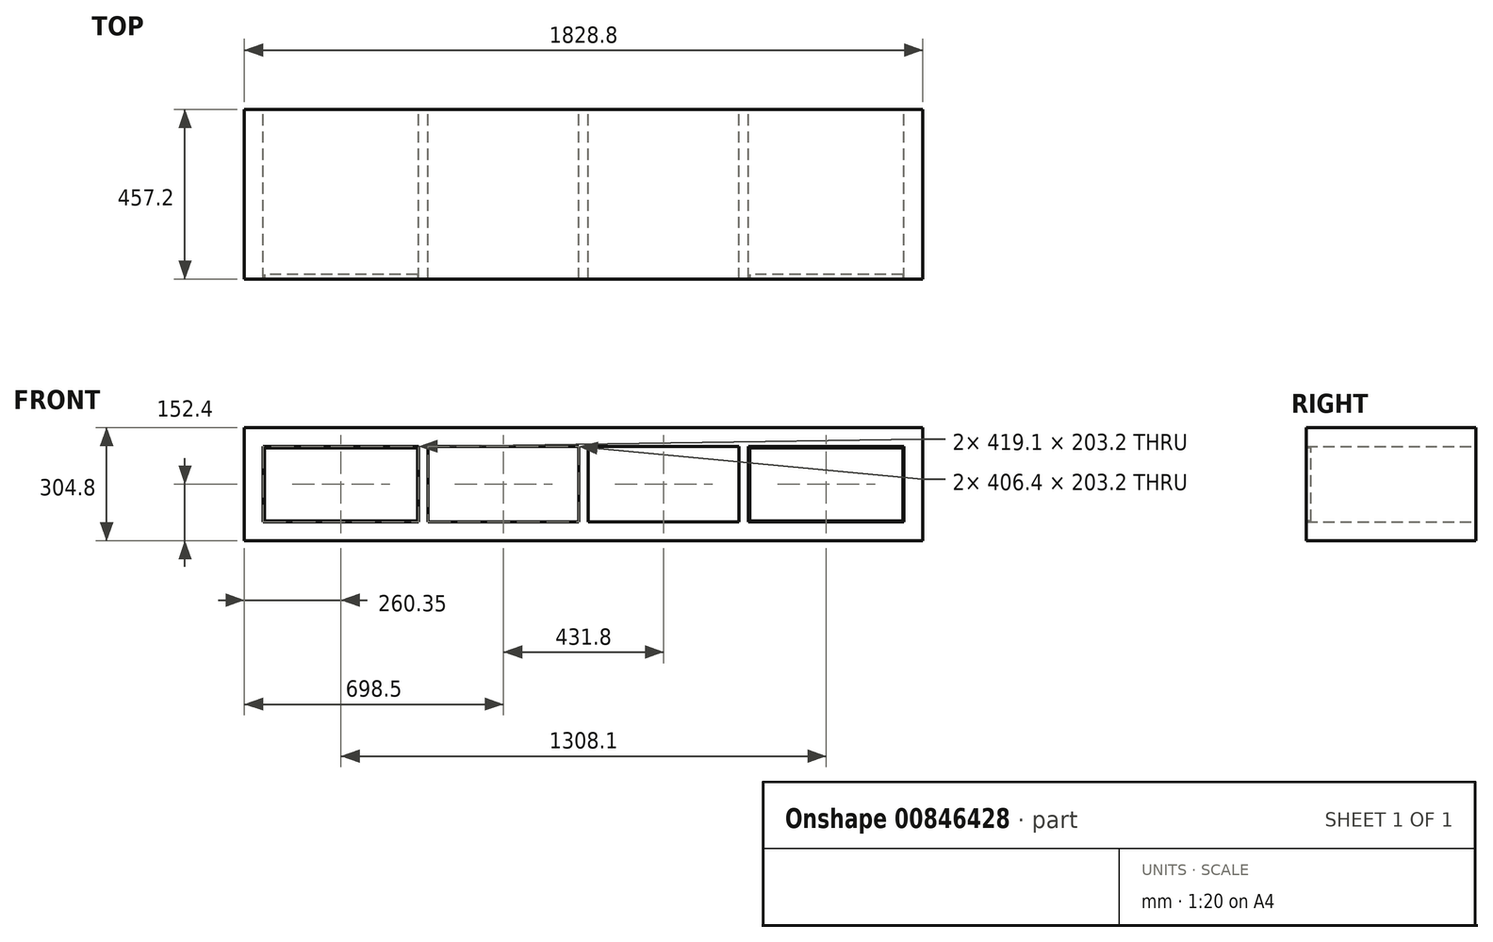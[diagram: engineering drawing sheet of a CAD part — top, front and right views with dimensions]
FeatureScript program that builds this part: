
annotation { "Feature Type Name" : "Feature", "Feature Type Description" : "" }
export const myFeature = defineFeature(function(context is Context, id is Id, definition is map)
    precondition{}
    {
        {
            var Q0;
            Q0=qCreatedBy(makeId("Front.planeOp"),FACE);
            var sketch = newSketch(context, id + "F0", { "sketchPlane" : qUnion([Q0])});
            skLineSegment(sketch, "E0.bottom", {"start": v(914.4, -152.4) * mm, "end": v(-914.4, -152.4) * mm});
            skLineSegment(sketch, "E0.top", {"start": v(914.4, 152.4) * mm, "end": v(-914.4, 152.4) * mm});
            skLineSegment(sketch, "E0.left", {"start": v(914.4, -152.4) * mm, "end": v(914.4, 152.4) * mm});
            skLineSegment(sketch, "E0.right", {"start": v(-914.4, -152.4) * mm, "end": v(-914.4, 152.4) * mm});
            skPoint(sketch, "E0.middle", {"position": v(0, 0) * mm});
            skLineSegment(sketch, "E1.0", {"start": v(-863.6, -101.6) * mm, "end": v(-863.6, 101.6) * mm});
            skLineSegment(sketch, "E1.1", {"start": v(863.6, -101.6) * mm, "end": v(-863.6, -101.6) * mm});
            skLineSegment(sketch, "E1.2", {"start": v(863.6, -101.6) * mm, "end": v(863.6, 101.6) * mm});
            skLineSegment(sketch, "E1.3", {"start": v(863.6, 101.6) * mm, "end": v(-863.6, 101.6) * mm});
            skLineSegment(sketch, "E2.0", {"start": v(444.5, -101.6) * mm, "end": v(444.5, 101.6) * mm});
            skLineSegment(sketch, "E3.0", {"start": v(419.1, -101.6) * mm, "end": v(419.1, 101.6) * mm});
            skLineSegment(sketch, "E4.0", {"start": v(12.7, -101.6) * mm, "end": v(12.7, 101.6) * mm});
            skLineSegment(sketch, "E5.0", {"start": v(-12.7, -101.6) * mm, "end": v(-12.7, 101.6) * mm});
            skLineSegment(sketch, "E6.0", {"start": v(-419.1, -101.6) * mm, "end": v(-419.1, 101.6) * mm});
            skLineSegment(sketch, "E7.0", {"start": v(-444.5, -101.6) * mm, "end": v(-444.5, 101.6) * mm});
            skSolve(sketch);
        }
        {
            var Q0;
            Q0=makeQuery(id+"F0.imprint","IMPRINT",FACE,{"disambiguationData":[TD([[makeQuery(id+"F0.imprint","IMPRINT",EDGE,{"derivedFrom":sQuery(id+"F0.wireOp",EDGE,"E0.bottom")}),-1.0]])]});
            var Q1;
            {var subQ0=sQuery(id+"F0.wireOp",EDGE,"E6.0");Q1=makeQuery(id+"F0.imprint","IMPRINT",FACE,{"disambiguationData":[TD([[makeQuery(id+"F0.imprint","IMPRINT",EDGE,{"derivedFrom":subQ0}),1.0]])]});}
            var Q2;
            {var subQ0=sQuery(id+"F0.wireOp",EDGE,"E4.0");Q2=makeQuery(id+"F0.imprint","IMPRINT",FACE,{"disambiguationData":[TD([[makeQuery(id+"F0.imprint","IMPRINT",EDGE,{"derivedFrom":subQ0}),1.0]])]});}
            var Q3;
            {var subQ0=sQuery(id+"F0.wireOp",EDGE,"E2.0");Q3=makeQuery(id+"F0.imprint","IMPRINT",FACE,{"disambiguationData":[TD([[makeQuery(id+"F0.imprint","IMPRINT",EDGE,{"derivedFrom":subQ0}),1.0]])]});}
            extrude(context, id + "F1", {"entities" : qUnion([Q0, Q1, Q2, Q3]), "depth" : 457.2 * mm, "offsetDistance" : 25.4 * mm});
        }
        {
            var Q0;
            Q0=makeQuery(id+"F1.opExtrude","CAP_FACE",FACE,{"disambiguationData":[OSD([sQuery(id+"F0.wireOp",EDGE,"E0.bottom"),sQuery(id+"F0.wireOp",EDGE,"E0.top"),sQuery(id+"F0.wireOp",EDGE,"E0.left"),sQuery(id+"F0.wireOp",EDGE,"E0.right"),sQuery(id+"F0.wireOp",EDGE,"E1.0"),sQuery(id+"F0.wireOp",EDGE,"E1.1"),sQuery(id+"F0.wireOp",EDGE,"E1.2"),sQuery(id+"F0.wireOp",EDGE,"E1.3"),sQuery(id+"F0.wireOp",EDGE,"E2.0"),sQuery(id+"F0.wireOp",EDGE,"E3.0"),sQuery(id+"F0.wireOp",EDGE,"E4.0"),sQuery(id+"F0.wireOp",EDGE,"E5.0"),sQuery(id+"F0.wireOp",EDGE,"E6.0"),sQuery(id+"F0.wireOp",EDGE,"E7.0")])],"isStart":false});
            var sketch = newSketch(context, id + "F2", { "sketchPlane" : qUnion([Q0])});
            skLineSegment(sketch, "E8.0", {"start": v(-447.67, 98.43) * mm, "end": v(-860.43, 98.43) * mm});
            skLineSegment(sketch, "E9.0", {"start": v(-860.43, -98.43) * mm, "end": v(-860.43, 98.43) * mm});
            skLineSegment(sketch, "E10.0", {"start": v(-447.67, -98.43) * mm, "end": v(-860.43, -98.43) * mm});
            skLineSegment(sketch, "E11.0", {"start": v(-447.67, -98.43) * mm, "end": v(-447.67, 98.43) * mm});
            skLineSegment(sketch, "E12.0", {"start": v(860.43, 98.43) * mm, "end": v(447.68, 98.43) * mm});
            skLineSegment(sketch, "E13.0", {"start": v(447.68, -98.43) * mm, "end": v(447.68, 98.43) * mm});
            skLineSegment(sketch, "E14.0", {"start": v(860.43, -98.42) * mm, "end": v(447.68, -98.43) * mm});
            skLineSegment(sketch, "E15.0", {"start": v(860.43, -98.42) * mm, "end": v(860.43, 98.43) * mm});
            skSolve(sketch);
        }
        {
            var Q0;
            Q0=makeQuery(id+"F2.imprint","IMPRINT",FACE,{"disambiguationData":[TD([[makeQuery(id+"F2.imprint","IMPRINT",EDGE,{"derivedFrom":sQuery(id+"F2.wireOp",EDGE,"E8.0")}),1.0]])]});
            extrude(context, id + "F3", {"entities" : qUnion([Q0]), "oppositeDirection" : true, "depth" : 12.7 * mm, "offsetDistance" : 25.4 * mm});
        }
        {
            var Q0;
            Q0 = qSketchRegion(id + "F2", true);
            extrude(context, id + "F4", {"entities" : qUnion([Q0]), "operationType" : NewBodyOperationType.ADD, "oppositeDirection" : true, "depth" : 12.7 * mm, "offsetDistance" : 25.4 * mm});
        }
    });
